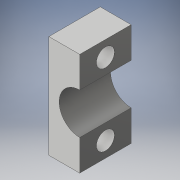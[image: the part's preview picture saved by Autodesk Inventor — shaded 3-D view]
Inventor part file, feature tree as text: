
AUTODESK INVENTOR PART (.ipt)
format: ipt  version: 2017 (Build 210142000, 142)  size: 128,512 bytes
history: native  units: mm
features: extrude x2, sketch x2, projected_geometry x2
ambient origin geometry x8: Origin, YZ Plane, XZ Plane, XY Plane, X Axis, Y Axis, Z Axis, Center Point
bodies: Solid1 (feature_tree)
feature tree (6):
  extrude  "Extrusion1"  Depth=20.0mm
  extrude  "Extrusion2"  Depth=20.0mm
  sketch  "Sketch1"  dims[d0=6.0mm d1=20.0mm]
  sketch  "Sketch2"  dims[d2=6.0mm d3=20.0mm d8=8.0mm d9=10.0mm d10=0.0mm d11=90.0deg d14=6.0mm d15=6.0mm d17=3.5mm d18=3.5mm d20=14.0mm d21=5.0mm d22=3.0mm d23=5.0mm d24=0.0mm d25=0.0mm]
  projected_geometry  "Projected Loop1"
  projected_geometry  "Projected Loop2"
